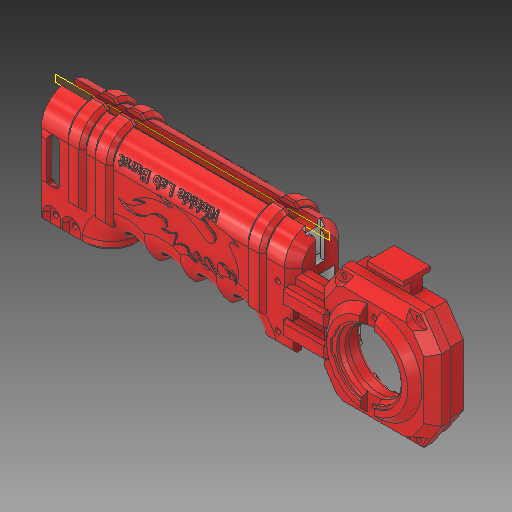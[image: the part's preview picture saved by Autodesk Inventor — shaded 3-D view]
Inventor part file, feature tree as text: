
AUTODESK INVENTOR PART (.ipt)
format: ipt  version: 2018 (Build 220112000, 112)  size: 8,896,512 bytes
history: native  units: mm
features: extrude x24, sketch x24, projected_geometry x8, other x3, mirror x2, chamfer x2, fillet x1
ambient origin geometry x8: Origin, YZ Plane, XZ Plane, XY Plane, X Axis, Y Axis, Z Axis, Center Point
bodies: Body1 (feature_tree)
feature tree (64):
  other  "ソリッド2"
  extrude  "押し出し1"  Depth=10.0mm TaperAngle=0.0deg
  extrude  "押し出し2"  Depth=10.0mm TaperAngle=0.0deg
  other  "作業平面1"
  extrude  "押し出し4"  Depth=3.5mm
  extrude  "押し出し5"  Depth=1.0mm TaperAngle=0.0deg
  extrude  "押し出し6"  Depth=25.0mm
  extrude  "押し出し7"  Depth=2.0mm TaperAngle=0.0deg
  extrude  "押し出し8"  Depth=2.0mm TaperAngle=0.0deg
  extrude  "押し出し10"  Depth=30.0mm
  extrude  "押し出し11"  Depth=11.0mm TaperAngle=0.0deg
  extrude  "押し出し12"  Depth=16.0mm
  extrude  "押し出し13"  Depth=30.0mm TaperAngle=0.0deg
  extrude  "押し出し17"  Depth=12.0mm
  extrude  "押し出し19"  Depth=19.0mm
  mirror  "ミラー2"
  extrude  "押し出し21"  Depth=2.5mm TaperAngle=0.0deg
  extrude  "押し出し22"  Depth=2.5mm TaperAngle=0.0deg
  extrude  "押し出し23"  Depth=2.5mm TaperAngle=0.0deg
  extrude  "押し出し24"  Depth=1.5mm TaperAngle=0.0deg
  chamfer  "面取り3"  Distance=2.0mm
  extrude  "押し出し25"  Depth=2.5mm
  chamfer  "面取り4"  Distance=2.5mm
  extrude  "押し出し26"  Depth=2.5mm
  extrude  "押し出し27"  Depth=2.5mm
  extrude  "押し出し28"  Depth=10.0mm TaperAngle=0.0deg
  extrude  "押し出し29"  TaperAngle=0.0deg  [1 undecoded]
  fillet  "フィレット3"  Radius=10.0mm
  extrude  "押し出し30"  Depth=21.0mm
  extrude  "押し出し31"  Depth=10.0mm TaperAngle=0.0deg
  mirror  "ミラー3"
  sketch  "スケッチ1"
  projected_geometry  "投影ループ1"
  sketch  "スケッチ2"
  projected_geometry  "投影ループ2"
  projected_geometry  "投影ループ3"
  sketch  "スケッチ5"
  sketch  "スケッチ6"
  sketch  "スケッチ7"
  sketch  "スケッチ8"
  sketch  "スケッチ9"
  sketch  "スケッチ11"
  sketch  "スケッチ12"
  sketch  "スケッチ13"
  projected_geometry  "投影ループ6"
  sketch  "スケッチ14"
  projected_geometry  "投影ループ7"
  sketch  "スケッチ18"
  projected_geometry  "投影ループ9"
  sketch  "スケッチ20"
  sketch  "スケッチ21"
  projected_geometry  "投影ループ11"
  sketch  "スケッチ22"
  sketch  "スケッチ23"
  sketch  "スケッチ24"
  sketch  "スケッチ25"
  sketch  "スケッチ26"
  sketch  "スケッチ27"
  projected_geometry  "投影ループ12"
  sketch  "スケッチ28"
  sketch  "スケッチ29"
  sketch  "スケッチ30"
  sketch  "スケッチ31"
  other  "ソリッド1"
note: 1 required parameter value undecoded (feature->parameter linkage not recoverable at this tier; creation-order binding heuristic only, values carry confidence <= 0.55)
